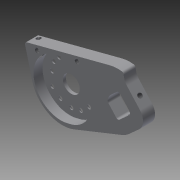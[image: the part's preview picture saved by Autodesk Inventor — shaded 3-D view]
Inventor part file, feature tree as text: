
AUTODESK INVENTOR PART (.ipt)
format: ipt  version: 2015 (Build 190159000, 159)  size: 375,296 bytes
history: native  units: in
note: dims shown in document units (in); Inventor stores cm internally (conversion verified against a paired STEP export)
features: sketch x9, extrude x7, thread x6, fillet x3, projected_geometry x3, other x1, chamfer x1
ambient origin geometry x8: Origin, YZ Plane, XZ Plane, XY Plane, X Axis, Y Axis, Z Axis, Center Point
bodies: Solid3 (feature_tree)
feature tree (30):
  other  "mountsketch_alt.ipt"
  extrude  "Extrusion11"  TaperAngle=360.0deg  [1 undecoded]
  fillet  "Fillet7"  Radius=0.5in
  sketch  "Sketch17"  dims[d94=0.1in d95=0.5in d99=0.19in d100=0.19in d101=0.355in]
  sketch  "Sketch12"  dims[d0=0.3937in]
  extrude  "Extrusion13"  Depth=1.0in
  extrude  "Extrusion14"  Depth=0.19in
  thread  "Thread5"  [1 undecoded]
  thread  "Thread6"  [1 undecoded]
  sketch  "Sketch16"  dims[d92=0.0in d93=1.0in]
  extrude  "Extrusion15"  Depth=1.0in TaperAngle=0.0deg
  fillet  "Fillet8"  Radius=1.0in
  fillet  "Fillet9"  Radius=1.0in
  sketch  "Sketch18"  dims[d102=0.25in d105=1.0in d106=0.0in d107=1.0in d108=0.0in d109=1.0in d110=0.0in]
  sketch  "Sketch19"  dims[d111=1.0in d112=0.0in d117=3.8981in d118=2.5984in]
  extrude  "Extrusion17"  Depth=3.8981in
  thread  "Thread7"  [1 undecoded]
  extrude  "Extrusion18"  TaperAngle=0.0deg  [1 undecoded]
  chamfer  "Chamfer1"  Distance=0.0938in
  thread  "Thread12"  [1 undecoded]
  thread  "Thread13"  [1 undecoded]
  extrude  "Extrusion21"  Depth=0.1in
  thread  "Thread14"  [1 undecoded]
  projected_geometry  "Projected Loop3"
  sketch  "Sketch13"  dims[d2=0.7087in d3=0.1693in d5=0.8661in d6=2.5984in d7=2.3827in d13=1.5748in d17=2.454in d18=1.9042in d15=360.0deg d91=0.5in]
  projected_geometry  "Projected Loop4"
  projected_geometry  "Projected Loop5"
  sketch  "Sketch21"  dims[d120=0.375in d121=0.0in]
  sketch  "Sketch22"  dims[d122=0.25in]
  sketch  "Sketch26"  dims[d123=0.2in d124=0.0938in d125=2.5984in d126=4.6599in d127=0.1in d128=2.5984in d129=4.7085in d136=0.5in d137=0.0in d138=0.19in d140=0.15in d142=1.0in d143=0.0in d146=2.5063in d147=0.9398in d148=2.2047in d149=0.19in d150=0.19in d153=0.5in d154=0.0in d161=0.0866in d162=0.125in d163=45.0deg d167=0.25in d178=2.2835in d179=2.2835in d181=0.5in d182=0.1875in d184=0.1875in d185=1.72in d188=1.0in d189=0.0in d190=1.0in d191=0.0in d192=0.19in d193=0.15in d194=0.15in d195=1.0in d196=0.0in d197=1.0in d198=0.0in]
note: 8 required parameter values undecoded (feature->parameter linkage not recoverable at this tier; creation-order binding heuristic only, values carry confidence <= 0.55)
